# Revit family: HVAC_HeatPumpAW_Enertech_CTC-EcoAir-600M
name_source: partatom
category: Specialty Equipment
units: mm (PartAtom-declared; Revit-internal decimal feet)

## family parameters
Always vertical = Yes
Cut with Voids When Loaded = No
OmniClass Number = 23.75.00.00
OmniClass Title = Climate Control (HVAC)
Part Type = Normal
Room Calculation Point = No
Round Connector Dimension = Use Diameter
Shared = No
Work Plane-Based = No

## types (2) — shared parameters
AirFlow max (m3/h) = 3129
AirFlow nominal (m3/h) = 2350
AssetType = Fixed
BIMObjectName = HVAC_HeatPumpAW_Enertech_CTC-EcoAir-600M
Brand = CTC
BrineSystem_Min_MaxPressure = 0-31
CO2Equivalent = 3.902
COP max: W35 & A +12 = 0.49
COP max: W35 & A +2 = 0.5
COP max: W35 & A +7 = 0.54
COP max: W35 & A -15 = 0
COP max: W35 & A -7 = 0
COP min: W35 & A +12 = 0.49
COP min: W35 & A +2 = 0.50
COP min: W35 & A +7 = 0.54
COP min: W35 & A -15 = 0
COP min: W35 & A -7 = 0
Capacity = Variable
Category = Heat Pumps, Air-to-water
Color = grey
DurationUnit = Year
EER max: A35 & W18 = 0
EER max: A35 & W7 = 0
EER min: A35 & W18 = 0
EER min: A35 & W7 = 0
EER nominal: A35 & W18 = 0
EER nominal: A35 & W7 = 0
ElectricalDeviceNominalPower = 0 W
EnergyClassHeatingWithControl W35 = A+++
EnergyClassHeatingWithoutControl W35 = A+++
EnergyClassHeatingWithoutControl W55 = A++
HasProtectiveEarth = Yes
IP_Code = IP X4
IfcExportAs = IfcElectricalDeviceCommon
IfcExportType = HEATER
InPutPower min: W35 & A +12 = 2920 W
InPutPower min: W35 & A +2 = 2170 W
InPutPower min: W35 & A +7 = 2550 W
InPutPower min: W35 & A -15 = 0 W
InPutPower min: W35 & A -7 = 0 W
KvsValueProduct = 5.5
Manufacturer = CTC AB
ManufacturerCountry = Sweden
ManufacturerName = CTC AB
ManufacturerURL = https://ctc.se
Material = Steel
MaxOperatingPressureThermalStore = 3
MaxStartingCurrent = 2.7
NBSDescription = Air to water heat pumps
NBSReference = 90-40-40/320
Name = CTC-EcoAir-600M
NominalCurrent = 0 A
NominalDepth = 545 mm
NominalFrequencyRange = 50 Hz
NominalHeight = 1080 mm  [stored 3.54331 ft]
NominalVoltage = 400 V
NominalWidth = 1245 mm
NumberOfPoles = 3
PhaseAngle = 0.00°
PowerFactor = 0 W
PumpMainMaterial = Steel - Grey
RatedHeatOutputCold Pdesigh W35 = 0 W
RatedHeatOutputCold Pdesigh W55 = 0 W
RatedHeatOutputModerate Pdesigh W35 = 0 W
RatedHeatOutputModerate Pdesigh W55 = 0 W
RatedHeatOutputWarm Pdesigh W35 = 0 W
RatedHeatOutputWarm Pdesigh W55 = 0 W
RatedVoltage = 1200 V
RefrigerantQuantity = 2.2
RefrigerantType = R407C
Revision = 6
Shape = Rectangular
Size = 545x1245x1080
Touchscreen = no
UNSPSCCode = 40101806
URL = https://ctc-heating.com
Uniclass2 = Pr_40_70_65
Uniclass2015Description = Preparation catering equipment
Uniclass2015Reference = Pr_40_70_65
UsageCurrent = 0 A
Version = 6
VersionDate = 13/05/2024
WarrantyDurationUnit = Year
WaterVolumeHeathingSystem = 1.9
Weight = 174
zero-valued in all types: Cost, Default Elevation

## per-type parameters (varying)
- CTC EcoAir 610M 3x400V3N: CoolingCapacity max: A35 & W18=7000 W; CoolingCapacity max: A35 & W7=7000 W; CoolingCapacity min: A35 & W18=7000 W; CoolingCapacity min: A35 & W7=7000 W; CoolingCapacity nominal: A35 & W18=6000 W; CoolingCapacity nominal: A35 & W7=7000 W; Description=CTC EcoAir 610M a speed controlled air-to-water heat pump,  which automatically adapts to the building's power demand during the year.; EANNumber=7333077087678; EnergyClassHeatingWithControl W55=A++; GroupFuse=10; InPutPower max: W35 & A +12=4600 W; InPutPower max: W35 & A +2=3250 W; InPutPower max: W35 & A +7=4040 W; InPutPower max: W35 & A -15=2350 W; InPutPower max: W35 & A -7=2820 W; Model=CTC EcoAir 610M; ModelNumber=588402001; ProductInformation=CTC EcoAir 610M a speed controlled air-to-water heat pump,  which automatically adapts to the building's power demand during the year.; RatedCurrent=7 A; SCOPCold W35=4.08; SCOPCold W55=4.08; SCOPModerate W35=4.81; SCOPModerate W55=4.81; SCOPWarm W35=5.91; SCOPWarm W55=5.91; Sound pressureLPA 10m=28; Sound pressureLPA 5m=34; SoundPowerLWA=53; SpecifiedOutput max: W35 & A +12=11050 W; SpecifiedOutput max: W35 & A +2=7080 W; SpecifiedOutput max: W35 & A +7=9610 W; SpecifiedOutput max: W35 & A -15=5010 W; SpecifiedOutput max: W35 & A -7=6200 W; SpecifiedOutput min: W35 & A +12=2400 W; SpecifiedOutput min: W35 & A +2=2180 W; SpecifiedOutput min: W35 & A +7=2380 W; SpecifiedOutput min: W35 & A -15=2130 W; SpecifiedOutput min: W35 & A -7=2200 W
- CTC EcoAir 614M 3x400V3N: CoolingCapacity max: A35 & W18=11000 W; CoolingCapacity max: A35 & W7=11000 W; CoolingCapacity min: A35 & W18=10000 W; CoolingCapacity min: A35 & W7=10000 W; CoolingCapacity nominal: A35 & W18=8000 W; CoolingCapacity nominal: A35 & W7=8000 W; Description=CTC EcoAir 614M a speed controlled air-to-water heat pump,  which automatically adapts to the building's power demand during the year.; EANNumber=7333077087654; EnergyClassHeatingWithControl W55=A+++; GroupFuse=13; InPutPower max: W35 & A +12=3240 W; InPutPower max: W35 & A +2=2630 W; InPutPower max: W35 & A +7=2920 W; InPutPower max: W35 & A -15=1980 W; InPutPower max: W35 & A -7=2210 W; Model=CTC EcoAir 614M; ModelNumber=588400001; ProductInformation=CTC EcoAir 614M a speed controlled air-to-water heat pump,  which automatically adapts to the building's power demand during the year.; RatedCurrent=10 A; SCOPCold W35=3.85; SCOPCold W55=3.85; SCOPModerate W35=4.90; SCOPModerate W55=4.90; SCOPWarm W35=5.87; SCOPWarm W55=5.87; Sound pressureLPA 10m=26; Sound pressureLPA 5m=32; SoundPowerLWA=51; SpecifiedOutput max: W35 & A +12=13340 W; SpecifiedOutput max: W35 & A +2=9660 W; SpecifiedOutput max: W35 & A +7=10790 W; SpecifiedOutput max: W35 & A -15=7570 W; SpecifiedOutput max: W35 & A -7=8690 W; SpecifiedOutput min: W35 & A +12=4120 W; SpecifiedOutput min: W35 & A +2=3670 W; SpecifiedOutput min: W35 & A +7=3700 W; SpecifiedOutput min: W35 & A -15=3820 W; SpecifiedOutput min: W35 & A -7=3940 W

note: [stored X ft] marks values corroborated as IEEE doubles in the binary element streams (Revit-internal decimal feet)

## geometry (parser evidence)
native form markers: Sweep x5
no freeform markers — native parametric forms only
